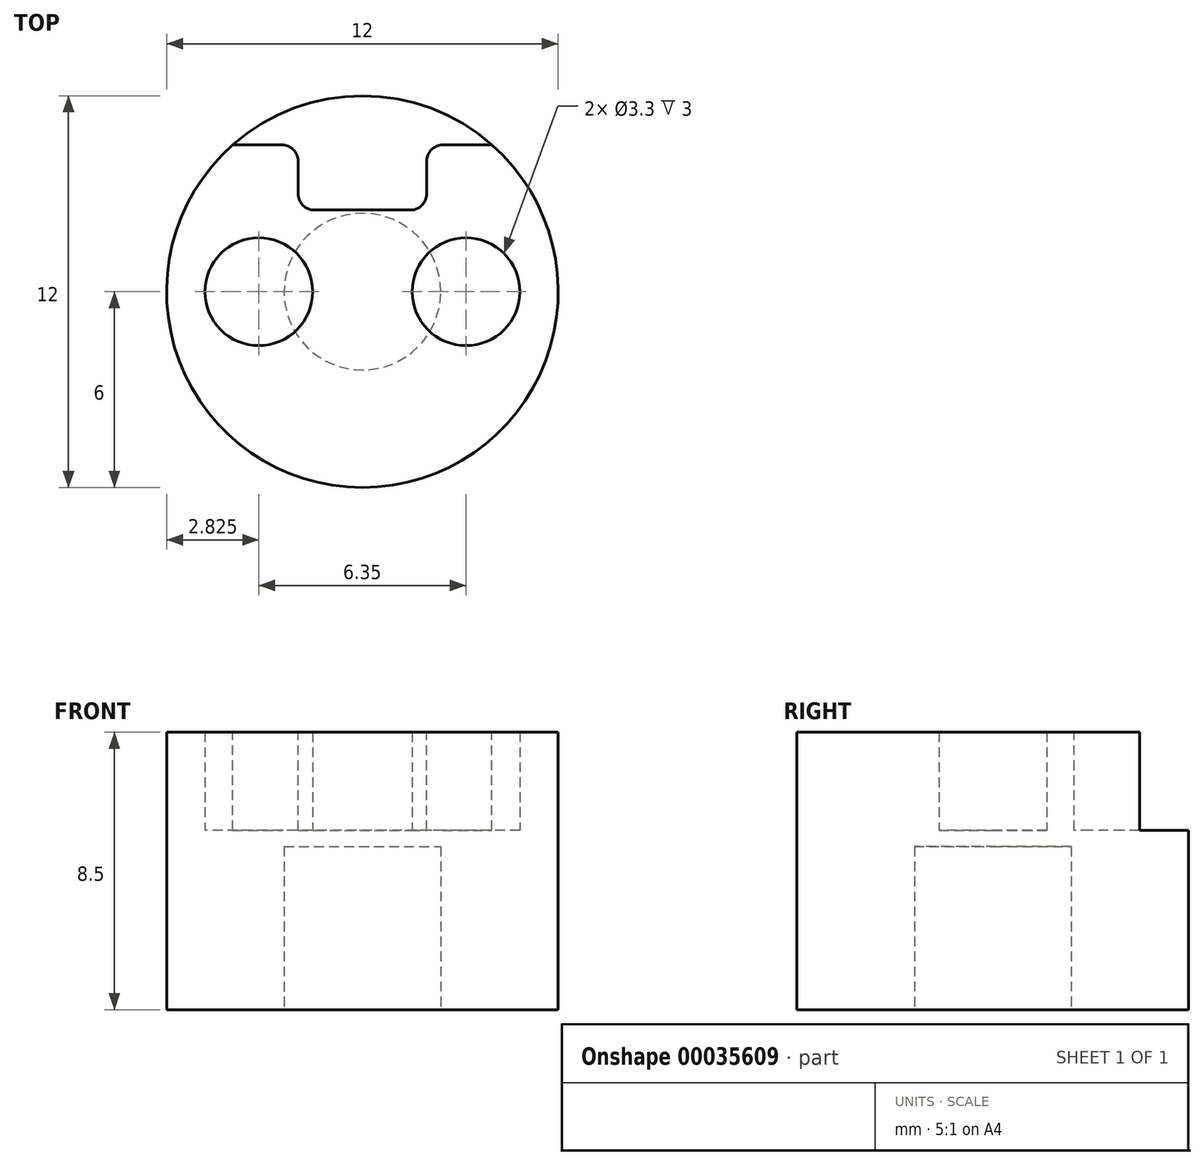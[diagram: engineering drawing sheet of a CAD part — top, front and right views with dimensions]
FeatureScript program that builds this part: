
annotation { "Feature Type Name" : "Feature", "Feature Type Description" : "" }
export const myFeature = defineFeature(function(context is Context, id is Id, definition is map)
    precondition{}
    {
        {
            var Q0;
            Q0=qCreatedBy(makeId("Top.planeOp"),FACE);
            var sketch = newSketch(context, id + "F0", { "sketchPlane" : qUnion([Q0])});
            skCircle(sketch, "E0", {"center": v(-3.18, 0) * mm, "radius": 1.65 * mm});
            skCircle(sketch, "E1", {"center": v(3.18, 0) * mm, "radius": 1.65 * mm});
            skCircle(sketch, "E2", {"center": v(0, 0) * mm, "radius": 6 * mm});
            skSolve(sketch);
        }
        {
            var Q0;
            Q0=qSketchRegion(id+"F0",true);
            extrude(context, id + "F1", {"entities" : qUnion([Q0]), "depth" : 3 * mm});
        }
        {
            var Q0;
            Q0=makeQuery(id+"F1.opExtrude","CAP_FACE",FACE,{"disambiguationData":[OSD([sQuery(id+"F0.wireOp",EDGE,"E0"),sQuery(id+"F0.wireOp",EDGE,"E1"),sQuery(id+"F0.wireOp",EDGE,"E2"),sQuery(id+"F0.wireOp",EDGE,"mxWlrIbW-bbLS-1jjZ-dLkJ-aSx3uFq2Umk3")])],"isStart":true});
            var sketch = newSketch(context, id + "F2", { "sketchPlane" : qUnion([Q0])});
            skCircle(sketch, "E3.0", {"center": v(0, 0) * mm, "radius": 6 * mm});
            skSolve(sketch);
        }
        {
            var Q0;
            Q0=qSketchRegion(id+"F2",true);
            extrude(context, id + "F3", {"entities" : qUnion([Q0]), "operationType" : NewBodyOperationType.ADD, "depth" : 5.5 * mm});
        }
        {
            var Q0;
            Q0=makeQuery(id+"F1.opExtrude","CAP_FACE",FACE,{"disambiguationData":[OSD([sQuery(id+"F0.wireOp",EDGE,"E0"),sQuery(id+"F0.wireOp",EDGE,"E1"),sQuery(id+"F0.wireOp",EDGE,"E2"),sQuery(id+"F0.wireOp",EDGE,"mxWlrIbW-bbLS-1jjZ-dLkJ-aSx3uFq2Umk3")])],"isStart":false});
            var sketch = newSketch(context, id + "F4", { "sketchPlane" : qUnion([Q0])});
            skLineSegment(sketch, "E4", {"start": v(-3.97, 4.5) * mm, "end": v(-1.97, 4.5) * mm});
            skLineSegment(sketch, "E5", {"start": v(-1.97, 4.5) * mm, "end": v(-1.97, 2.5) * mm});
            skLineSegment(sketch, "E6", {"start": v(-1.97, 2.5) * mm, "end": v(1.97, 2.5) * mm});
            skLineSegment(sketch, "E7", {"start": v(1.97, 2.5) * mm, "end": v(1.97, 4.5) * mm});
            skLineSegment(sketch, "E8", {"start": v(1.97, 4.5) * mm, "end": v(3.97, 4.5) * mm});
            skCircle(sketch, "E9.0", {"center": v(0, 0) * mm, "radius": 6 * mm});
            skSolve(sketch);
        }
        {
            var Q0;
            {var subQ1=sQuery(id+"F4.wireOp",EDGE,"E4");Q0=makeQuery(id+"F4.imprint","IMPRINT",FACE,{"disambiguationData":[TD([[makeQuery(id+"F4.imprint","IMPRINT",EDGE,{"derivedFrom":subQ1}),1.0]])]});}
            extrude(context, id + "F5", {"entities" : qUnion([Q0]), "operationType" : NewBodyOperationType.REMOVE, "oppositeDirection" : true, "depth" : 3 * mm});
        }
        {
            var Q0;
            Q0=makeQuery(id+"F5.boolean.opBoolean","COPY",EDGE,{"derivedFrom":makeQuery(id+"F5.opExtrude","SWEPT_EDGE",EDGE,{"disambiguationData":[OSD([sQuery(id+"F4.wireOp",EDGE,"E4"),sQuery(id+"F4.wireOp",EDGE,"E9.0")])]})});
            var Q1;
            Q1=makeQuery(id+"F5.boolean.opBoolean","COPY",EDGE,{"derivedFrom":makeQuery(id+"F5.opExtrude","SWEPT_EDGE",EDGE,{"disambiguationData":[OSD([sQuery(id+"F4.wireOp",EDGE,"E4"),sQuery(id+"F4.wireOp",EDGE,"E5")])]})});
            var Q2;
            Q2=makeQuery(id+"F5.boolean.opBoolean","COPY",EDGE,{"derivedFrom":makeQuery(id+"F5.opExtrude","SWEPT_EDGE",EDGE,{"disambiguationData":[OSD([sQuery(id+"F4.wireOp",EDGE,"E6"),sQuery(id+"F4.wireOp",EDGE,"E7")])]})});
            var Q3;
            Q3=makeQuery(id+"F5.boolean.opBoolean","COPY",EDGE,{"derivedFrom":makeQuery(id+"F5.opExtrude","SWEPT_EDGE",EDGE,{"disambiguationData":[OSD([sQuery(id+"F4.wireOp",EDGE,"E7"),sQuery(id+"F4.wireOp",EDGE,"E8")])]})});
            var Q4;
            Q4=makeQuery(id+"F5.boolean.opBoolean","COPY",EDGE,{"derivedFrom":makeQuery(id+"F5.opExtrude","SWEPT_EDGE",EDGE,{"disambiguationData":[OSD([sQuery(id+"F4.wireOp",EDGE,"E8"),sQuery(id+"F4.wireOp",EDGE,"E9.0")])]})});
            var Q5;
            Q5=makeQuery(id+"F5.boolean.opBoolean","COPY",EDGE,{"derivedFrom":makeQuery(id+"F5.opExtrude","SWEPT_EDGE",EDGE,{"disambiguationData":[OSD([sQuery(id+"F4.wireOp",EDGE,"E5"),sQuery(id+"F4.wireOp",EDGE,"E6")])]})});
            fillet(context, id + "F6", {"entities" : qUnion([Q0, Q1, Q2, Q3, Q4, Q5]), "radius" : .5 * mm, "tangentPropagation" : true, "allowEdgeOverflow" : false});
        }
        {
            var Q0;
            Q0=makeQuery(id+"F3.opExtrude","CAP_FACE",FACE,{"disambiguationData":[OSD([sQuery(id+"F2.wireOp",EDGE,"E3.0")])],"isStart":false});
            var sketch = newSketch(context, id + "F7", { "sketchPlane" : qUnion([Q0])});
            skCircle(sketch, "E10", {"center": v(0, 0) * mm, "radius": 2.4 * mm});
            skSolve(sketch);
        }
        {
            var Q0;
            Q0=qSketchRegion(id+"F7",true);
            extrude(context, id + "F8", {"entities" : qUnion([Q0]), "operationType" : NewBodyOperationType.REMOVE, "oppositeDirection" : true, "depth" : 5 * mm, "offsetDistance" : 25 * mm});
        }
    });
